FCSTD DOCUMENT  (FreeCAD 0.19R)
Label: HDprac
License: All rights reserved
LicenseURL: http://en.wikipedia.org/wiki/All_rights_reserved
objects: Part::Cylinder×62, Part::Refine×28, Part::Feature×24, Part::MultiFuse×22, Part::Cut×20, Part::FeaturePython×14, Part::Chamfer×9, App::Part×2, Part::Box×1
note: 180 computed .brp shape members not serialized (recipe doc carries the construction recipe); baked Part::Feature solids carry a one-line shape summary decoded from their .brp

FEATURE [Part::Feature] Part__Feature048  label="OUTPUT_SHAFT"
  Placement = pos=(0,0,-16) rot=(1,0,0;1.5708rad)
  shape: bbox 70.02 x 70.02 x 15.12 mm, 150 faces (baked)
FEATURE [Part::Feature] Part__Feature015  label="CIRCULAR_SPLINE"
  Placement = pos=(-3.943e-12,44,4.322e-12) rot=(1,0,0;3.14159rad)
  shape: bbox 100 x 10 x 100 mm, 706 faces (baked)
FEATURE [Part::Feature] Part__Feature014  label="FLEXGEAR"
  Placement = pos=(0,33.5,0) rot=(0,0,1;0rad)
  shape: bbox 81.18 x 57.96 x 81.18 mm, 699 faces (baked)
FEATURE [Part::FeaturePython] cycloidgear  # WARN: FeaturePython — macro-defined, semantics opaque (R4)
  AttacherType = Attacher::AttachEngine3D
  Placement = pos=(0,44,0) rot=(1,0,0;1.5708rad)
  backlash = 0
  beta = 0
  clearance = 0.25
  double_helix = false
  head = 0
  height = 10
  inner_diameter = 5
  module = 1
  numpoints = 15
  outer_diameter = 5
  teeth = 79
  version = 0.0.3
FEATURE [Part::Cylinder] Cylinder  label="Válec"
  Angle = 360
  AttacherType = Attacher::AttachEngine3D
  Height = 10
  Placement = pos=(0,44,0) rot=(1,0,0;1.5708rad)
  Radius = 50
FEATURE [Part::Cylinder] Cylinder001  label="Válec001"
  Angle = 360
  AttacherType = Attacher::AttachEngine3D
  Height = 10
  Placement = pos=(0,44,45.4) rot=(1,0,0;1.5708rad)
  Radius = 2.15
FEATURE [Part::Refine] Cylinder001001  label="Válec002"
  Placement = pos=(0,0,0) rot=(0,1,0;1.0472rad)
  Source = -> Cylinder001
FEATURE [Part::Refine] Cylinder001002  label="Válec003"
  Placement = pos=(0,0,0) rot=(0,1,0;2.0944rad)
  Source = -> Cylinder001
FEATURE [Part::Refine] Cylinder001003  label="Válec004"
  Placement = pos=(0,0,0) rot=(0,1,0;3.14159rad)
  Source = -> Cylinder001
FEATURE [Part::Refine] Cylinder001004  label="Válec005"
  Placement = pos=(0,0,0) rot=(0,1,0;4.18879rad)
  Source = -> Cylinder001
FEATURE [Part::Refine] Cylinder001005  label="Válec006"
  Placement = pos=(0,0,0) rot=(0,-1,0;1.0472rad)
  Source = -> Cylinder001
FEATURE [Part::MultiFuse] Fusion
  Shapes = -> [cycloidgear,Cylinder001,Cylinder001001,Cylinder001002,Cylinder001003,Cylinder001004,Cylinder001005]
FEATURE [Part::Chamfer] Chamfer
  Base = -> Cylinder
  Edges = 2 edges r=1: [Edge1,Edge3]
FEATURE [Part::Cut] Cut  label="CIRCULAR_79"
  Base = -> Chamfer
  Tool = -> Fusion
FEATURE [Part::Cylinder] Cylinder001006  label="Válec007"
  Angle = 360
  AttacherType = Attacher::AttachEngine3D
  Height = 10
  Placement = pos=(0,44,0) rot=(1,0,0;1.5708rad)
  Radius = 50
FEATURE [Part::FeaturePython] cycloidgear001  # WARN: FeaturePython — macro-defined, semantics opaque (R4)
  AttacherType = Attacher::AttachEngine3D
  Placement = pos=(0,43.5,0) rot=(1,0,0;1.5708rad)
  backlash = 0
  beta = 0
  clearance = 0.25
  double_helix = false
  head = 0
  height = 11
  inner_diameter = 5
  module = 0.55
  numpoints = 15
  outer_diameter = 5
  teeth = 145
  version = 0.0.3
FEATURE [Part::Cylinder] Cylinder001007  label="Válec008"
  Angle = 360
  AttacherType = Attacher::AttachEngine3D
  Height = 10
  Placement = pos=(0,44,45.4) rot=(1,0,0;1.5708rad)
  Radius = 2.15
FEATURE [Part::Chamfer] Chamfer001
  Base = -> Cylinder001006
  Edges = 2 edges r=1: [Edge1,Edge3]
FEATURE [Part::Refine] Cylinder001008  label="Válec009"
  Placement = pos=(0,0,0) rot=(0,1,0;2.0944rad)
  Source = -> Cylinder001007
FEATURE [Part::Refine] Cylinder001009  label="Válec010"
  Placement = pos=(0,0,0) rot=(0,1,0;1.0472rad)
  Source = -> Cylinder001007
FEATURE [Part::Refine] Cylinder001010  label="Válec011"
  Placement = pos=(0,0,0) rot=(0,1,0;4.18879rad)
  Source = -> Cylinder001007
FEATURE [Part::Refine] Cylinder001011  label="Válec012"
  Placement = pos=(0,0,0) rot=(0,-1,0;1.0472rad)
  Source = -> Cylinder001007
FEATURE [Part::Refine] Cylinder001012  label="Válec013"
  Placement = pos=(0,0,0) rot=(0,1,0;3.14159rad)
  Source = -> Cylinder001007
FEATURE [Part::MultiFuse] Fusion001
  Shapes = -> [cycloidgear001,Cylinder001007,Cylinder001009,Cylinder001008,Cylinder001012,Cylinder001010,Cylinder001011]
FEATURE [Part::Cut] Cut001  label="CIRCULAR_145"
  Base = -> Chamfer001
  Tool = -> Fusion001
FEATURE [Part::Cylinder] Cylinder001014  label="Válec015"
  Angle = 360
  AttacherType = Attacher::AttachEngine3D
  Height = 10
  Placement = pos=(0,44,0) rot=(1,0,0;1.5708rad)
  Radius = 50
FEATURE [Part::Cylinder] Cylinder001017  label="Válec018"
  Angle = 360
  AttacherType = Attacher::AttachEngine3D
  Height = 10
  Placement = pos=(0,44,45.4) rot=(1,0,0;1.5708rad)
  Radius = 2.15
FEATURE [Part::Refine] Cylinder001013  label="Válec014"
  Placement = pos=(0,0,0) rot=(0,-1,0;1.0472rad)
  Source = -> Cylinder001017
FEATURE [Part::Refine] Cylinder001015  label="Válec016"
  Placement = pos=(0,0,0) rot=(0,1,0;2.0944rad)
  Source = -> Cylinder001017
FEATURE [Part::Refine] Cylinder001016  label="Válec017"
  Placement = pos=(0,0,0) rot=(0,1,0;4.18879rad)
  Source = -> Cylinder001017
FEATURE [Part::FeaturePython] cycloidgear002  # WARN: FeaturePython — macro-defined, semantics opaque (R4)
  AttacherType = Attacher::AttachEngine3D
  Placement = pos=(0,44,0) rot=(1,0,0;1.5708rad)
  backlash = 0
  beta = 30
  clearance = 0.25
  double_helix = false
  head = 0
  height = 10
  inner_diameter = 5
  module = 0.792
  numpoints = 15
  outer_diameter = 5
  teeth = 101
  version = 0.0.3
FEATURE [Part::Chamfer] Chamfer002
  Base = -> Cylinder001014
  Edges = 2 edges r=1: [Edge1,Edge3]
FEATURE [Part::Refine] Cylinder001018  label="Válec019"
  Placement = pos=(0,0,0) rot=(0,1,0;1.0472rad)
  Source = -> Cylinder001017
FEATURE [Part::Refine] Cylinder001019  label="Válec020"
  Placement = pos=(0,0,0) rot=(0,1,0;3.14159rad)
  Source = -> Cylinder001017
FEATURE [Part::MultiFuse] Fusion002
  Shapes = -> [cycloidgear002,Cylinder001017,Cylinder001018,Cylinder001015,Cylinder001019,Cylinder001016,Cylinder001013]
FEATURE [Part::Cut] Cut002  label="CIRCULAR_101"
  Base = -> Chamfer002
  Tool = -> Fusion002
FEATURE [Part::FeaturePython] cycloidgear003  # WARN: FeaturePython — macro-defined, semantics opaque (R4)
  AttacherType = Attacher::AttachEngine3D
  Placement = pos=(0,44,0) rot=(1,0,0;1.5708rad)
  backlash = 0
  beta = 30
  clearance = 0.25
  double_helix = false
  head = 0
  height = 11
  inner_diameter = 5
  module = 0.792
  numpoints = 15
  outer_diameter = 5
  teeth = 101
  version = 0.0.3
FEATURE [Part::Cylinder] Cylinder001023  label="Válec024"
  Angle = 360
  AttacherType = Attacher::AttachEngine3D
  Height = 10
  Placement = pos=(0,44,45.4) rot=(1,0,0;1.5708rad)
  Radius = 2.15
FEATURE [Part::Refine] Cylinder001020  label="Válec021"
  Placement = pos=(0,0,0) rot=(0,1,0;4.18879rad)
  Source = -> Cylinder001023
FEATURE [Part::Refine] Cylinder001021  label="Válec022"
  Placement = pos=(0,0,0) rot=(0,-1,0;1.0472rad)
  Source = -> Cylinder001023
FEATURE [Part::Refine] Cylinder001022  label="Válec023"
  Placement = pos=(0,0,0) rot=(0,1,0;2.0944rad)
  Source = -> Cylinder001023
FEATURE [Part::Refine] Cylinder001024  label="Válec025"
  Placement = pos=(0,0,0) rot=(0,1,0;3.14159rad)
  Source = -> Cylinder001023
FEATURE [Part::Refine] Cylinder001025  label="Válec026"
  Placement = pos=(0,0,0) rot=(0,1,0;1.0472rad)
  Source = -> Cylinder001023
FEATURE [Part::MultiFuse] Fusion003
  Shapes = -> [cycloidgear003,Cylinder001023,Cylinder001025,Cylinder001022,Cylinder001024,Cylinder001020,Cylinder001021]
FEATURE [Part::Cylinder] Cylinder001026  label="Válec027"
  Angle = 360
  AttacherType = Attacher::AttachEngine3D
  Height = 10
  Placement = pos=(0,44,0) rot=(1,0,0;1.5708rad)
  Radius = 50
FEATURE [Part::Chamfer] Chamfer003
  Base = -> Cylinder001026
  Edges = 2 edges r=1: [Edge1,Edge3]
FEATURE [Part::Cut] Cut003
  Base = -> Chamfer003
  Tool = -> Fusion003
FEATURE [Part::Cylinder] cylinder
  Angle = 360
  AttacherType = Attacher::AttachEngine3D
  Height = 10
  Radius = 3
FEATURE [Part::Cylinder] cylinder001
  Angle = 360
  AttacherType = Attacher::AttachEngine3D
  Height = 10
  Placement = pos=(15,0,0) rot=(0,0,1;0rad)
  Radius = 3.5
FEATURE [Part::Cylinder] cylinder002
  Angle = 360
  AttacherType = Attacher::AttachEngine3D
  Height = 5
  Placement = pos=(15,0,0) rot=(0,0,1;0rad)
  Radius = 7
FEATURE [Part::Cylinder] cylinder003
  Angle = 360
  AttacherType = Attacher::AttachEngine3D
  Height = 10
  Placement = pos=(-15,0,0) rot=(0,0,1;0rad)
  Radius = 3.5
FEATURE [Part::Cylinder] cylinder004
  Angle = 360
  AttacherType = Attacher::AttachEngine3D
  Height = 5
  Placement = pos=(-15,0,0) rot=(0,0,1;0rad)
  Radius = 7
FEATURE [Part::Cylinder] cylinder005
  Angle = 360
  AttacherType = Attacher::AttachEngine3D
  Height = 10
  Placement = pos=(-25,0,0) rot=(0,0,1;0rad)
  Radius = 2.6
FEATURE [Part::Cylinder] cylinder006
  Angle = 360
  AttacherType = Attacher::AttachEngine3D
  Height = 10
  Placement = pos=(25,0,0) rot=(0,0,1;0rad)
  Radius = 2.6
FEATURE [Part::MultiFuse] union
  Shapes = -> [cylinder,cylinder001,cylinder002,cylinder003,cylinder004,cylinder005,cylinder006]
FEATURE [Part::Cylinder] Cylinder001027  label="Válec028"
  Angle = 360
  AttacherType = Attacher::AttachEngine3D
  Height = 10
  Radius = 35
FEATURE [Part::Cut] Cut004  label="H1"
  Base = -> Cylinder001027
  Placement = pos=(0,0,10) rot=(0,0,1;0rad)
  Tool = -> union
FEATURE [Part::Cylinder] Cylinder001028  label="H2"
  Angle = 360
  AttacherType = Attacher::AttachEngine3D
  Height = 10
  Radius = 35
FEATURE [Part::Cylinder] Cylinder001029  label="Válec030"
  Angle = 360
  AttacherType = Attacher::AttachEngine3D
  Height = 16
  Placement = pos=(0,24,-6) rot=(0,0,1;0rad)
  Radius = 2.15
FEATURE [Part::Cylinder] cylinder007
  Angle = 360
  AttacherType = Attacher::AttachEngine3D
  Height = 10
  Placement = pos=(-25,0,0) rot=(0,0,1;0rad)
  Radius = 2.6
FEATURE [Part::Cylinder] cylinder008
  Angle = 360
  AttacherType = Attacher::AttachEngine3D
  Height = 10
  Placement = pos=(25,0,0) rot=(0,0,1;0rad)
  Radius = 2.6
FEATURE [Part::Cylinder] cylinder009
  Angle = 360
  AttacherType = Attacher::AttachEngine3D
  Height = 10
  Radius = 3
FEATURE [Part::Cylinder] Cylinder001030  label="Válec031"
  Angle = 360
  AttacherType = Attacher::AttachEngine3D
  Height = 4
  Placement = pos=(0,24,6) rot=(0,0,1;0rad)
  Radius = 3.6
FEATURE [Part::MultiFuse] Fusion004  label="Imbus"
  Shapes = -> [Cylinder001030,Cylinder001029]
FEATURE [Part::Refine] Fusion004001  label="Imbus001"
  Placement = pos=(0,0,0) rot=(0,0,1;1.0472rad)
  Source = -> Fusion004
FEATURE [Part::Refine] Fusion004002  label="Imbus002"
  Placement = pos=(0,0,0) rot=(0,0,1;2.0944rad)
  Source = -> Fusion004
FEATURE [Part::Refine] Fusion004003  label="Imbus003"
  Placement = pos=(0,0,0) rot=(0,0,1;3.14159rad)
  Source = -> Fusion004
FEATURE [Part::Refine] Fusion004004  label="Imbus004"
  Placement = pos=(0,0,0) rot=(0,0,1;4.18879rad)
  Source = -> Fusion004
FEATURE [Part::Refine] Fusion004005  label="Imbus005"
  Placement = pos=(0,0,0) rot=(0,0,-1;1.0472rad)
  Source = -> Fusion004
FEATURE [Part::FeaturePython] Nut  label="M5-Nut"  # Fasteners workbench fastener (typed FeaturePython)
  Placement = pos=(25,0,0) rot=(0.894427,0,0.447214;0rad)
  diameter = 7
  invert = false
  matchOuter = false
  offset = 0
  thread = false
  type = 7
FEATURE [Part::FeaturePython] Nut001  label="M5-Nut001"  # Fasteners workbench fastener (typed FeaturePython)
  Placement = pos=(-25,0,0) rot=(0.894427,0,0.447214;0rad)
  diameter = 7
  invert = false
  matchOuter = false
  offset = 0
  thread = false
  type = 7
FEATURE [Part::MultiFuse] Fusion004006
  Shapes = -> [cylinder007,cylinder008,cylinder009,Fusion004,Fusion004001,Fusion004002,Fusion004003,Fusion004004,Fusion004005,Nut,Nut001]
FEATURE [Part::Cut] Cut005
  Base = -> Cylinder001028
  Tool = -> Fusion004006
FEATURE [Part::Chamfer] Chamfer004  label="HH1"
  Base = -> Cut004
  Edges = 2 edges r=1: [Edge1,Edge3]
FEATURE [Part::Chamfer] Chamfer005  label="HH2"
  Base = -> Cut005
  Edges = 2 edges r=1: [Edge1,Edge3]
FEATURE [Part::Feature] Part__Feature049  label="FLEXGEAR001"
  Placement = pos=(0,33.5,0) rot=(0,0,1;0rad)
  shape: bbox 81.18 x 57.96 x 81.18 mm, 699 faces (baked)
FEATURE [Part::FeaturePython] cycloidgear005  # WARN: FeaturePython — macro-defined, semantics opaque (R4)
  AttacherType = Attacher::AttachEngine3D
  Placement = pos=(0,43.5,0) rot=(1,0,0;1.5708rad)
  backlash = 0
  beta = 0
  clearance = 0.25
  double_helix = false
  head = 0
  height = 10.5
  inner_diameter = 5
  module = 0.79
  numpoints = 15
  outer_diameter = 5
  teeth = 100
  version = 0.0.3
FEATURE [Part::FeaturePython] Tube  # WARN: FeaturePython — macro-defined, semantics opaque (R4)
  AttacherType = Attacher::AttachEngine3D
  Height = 10
  InnerRadius = 36.5
  OuterRadius = 42
  Placement = pos=(0,35.75,0) rot=(1,0,0;1.5708rad)
FEATURE [Part::Chamfer] Chamfer007
  Base = -> Tube
  Edges = 1 edges r=4: [Edge5]
FEATURE [Part::Cut] Cut007
  Base = -> cycloidgear005
  Tool = -> Chamfer007
FEATURE [Part::Cylinder] Cylinder001038  label="Válec039"
  Angle = 360
  AttacherType = Attacher::AttachEngine3D
  Height = 10.5
  Placement = pos=(0,43.5,0) rot=(1,0,0;1.5708rad)
  Radius = 42
FEATURE [Part::Cylinder] Cylinder001039  label="Válec040"
  Angle = 360
  AttacherType = Attacher::AttachEngine3D
  Height = 10.5
  Placement = pos=(0,43.5,0) rot=(1,0,0;1.5708rad)
  Radius = 36.3
FEATURE [Part::Cut] Cut008
  Base = -> Part__Feature049
  Tool = -> Cylinder001038
FEATURE [Part::MultiFuse] Fusion004008
  Shapes = -> [Cut007,Cut008]
FEATURE [Part::Cut] Cut009  label="FLEX100"
  Base = -> Fusion004008
  Tool = -> Cylinder001039
FEATURE [Part::Refine] Cut009001  label="FLEX100n"
  Source = -> Cut009
FEATURE [Part::FeaturePython] cycloidgear006  # WARN: FeaturePython — macro-defined, semantics opaque (R4)
  AttacherType = Attacher::AttachEngine3D
  Placement = pos=(0,43.5,0) rot=(1,0,0;1.5708rad)
  backlash = 0
  beta = 0
  clearance = 0.25
  double_helix = false
  head = 0
  height = 10.5
  inner_diameter = 5
  module = 1
  numpoints = 15
  outer_diameter = 5
  teeth = 78
  version = 0.0.3
FEATURE [Part::Feature] Part__Feature050  label="FLEXGEAR002"
  Placement = pos=(0,33.5,0) rot=(0,0,1;0rad)
  shape: bbox 81.18 x 57.96 x 81.18 mm, 699 faces (baked)
FEATURE [Part::FeaturePython] Tube001  # WARN: FeaturePython — macro-defined, semantics opaque (R4)
  AttacherType = Attacher::AttachEngine3D
  Height = 10
  InnerRadius = 36.5
  OuterRadius = 42
  Placement = pos=(0,35.75,0) rot=(1,0,0;1.5708rad)
FEATURE [Part::Chamfer] Chamfer008
  Base = -> Tube001
  Edges = 1 edges r=4: [Edge5]
FEATURE [Part::Cut] Cut009002
  Base = -> cycloidgear006
  Tool = -> Chamfer008
FEATURE [Part::Cylinder] Cylinder001040  label="Válec041"
  Angle = 360
  AttacherType = Attacher::AttachEngine3D
  Height = 11.5
  Placement = pos=(0,43.5,0) rot=(1,0,0;1.5708rad)
  Radius = 36.3
FEATURE [Part::Cylinder] Cylinder001041  label="Válec042"
  Angle = 360
  AttacherType = Attacher::AttachEngine3D
  Height = 10.5
  Placement = pos=(0,43.5,0) rot=(1,0,0;1.5708rad)
  Radius = 42
FEATURE [Part::Cut] Cut009004
  Base = -> Part__Feature050
  Tool = -> Cylinder001041
FEATURE [Part::MultiFuse] Fusion004009
  Shapes = -> [Cut009002,Cut009004]
FEATURE [Part::Cut] Cut009003  label="FLEX78"
  Base = -> Fusion004009
  Tool = -> Cylinder001040
FEATURE [Part::Refine] Cut009003001  label="FLEX78n"
  Source = -> Cut009003
FEATURE [Part::FeaturePython] cycloidgear007  # WARN: FeaturePython — macro-defined, semantics opaque (R4)
  AttacherType = Attacher::AttachEngine3D
  Placement = pos=(0,43.5,0) rot=(1,0,0;1.5708rad)
  backlash = 0
  beta = 0
  clearance = 0.25
  double_helix = false
  head = 0
  height = 10.5
  inner_diameter = 5
  module = 0.55
  numpoints = 15
  outer_diameter = 5
  teeth = 144
  version = 0.0.3
FEATURE [Part::Feature] Part__Feature051  label="FLEXGEAR003"
  Placement = pos=(0,33.5,0) rot=(0,0,1;0rad)
  shape: bbox 81.18 x 57.96 x 81.18 mm, 699 faces (baked)
FEATURE [Part::FeaturePython] Tube002  # WARN: FeaturePython — macro-defined, semantics opaque (R4)
  AttacherType = Attacher::AttachEngine3D
  Height = 10
  InnerRadius = 36.5
  OuterRadius = 42
  Placement = pos=(0,35.75,0) rot=(1,0,0;1.5708rad)
FEATURE [Part::Chamfer] Chamfer009
  Base = -> Tube002
  Edges = 1 edges r=4: [Edge5]
FEATURE [Part::Cut] Cut009003002
  Base = -> cycloidgear007
  Tool = -> Chamfer009
FEATURE [Part::Cylinder] Cylinder001042  label="Válec043"
  Angle = 360
  AttacherType = Attacher::AttachEngine3D
  Height = 11.5
  Placement = pos=(0,43.5,0) rot=(1,0,0;1.5708rad)
  Radius = 36.3
FEATURE [Part::Cylinder] Cylinder001043  label="Válec044"
  Angle = 360
  AttacherType = Attacher::AttachEngine3D
  Height = 10.5
  Placement = pos=(0,43.5,0) rot=(1,0,0;1.5708rad)
  Radius = 42
FEATURE [Part::Cut] Cut009003004
  Base = -> Part__Feature051
  Tool = -> Cylinder001043
FEATURE [Part::MultiFuse] Fusion004010
  Shapes = -> [Cut009003002,Cut009003004]
FEATURE [Part::Cut] Cut009003003  label="FLEX144"
  Base = -> Fusion004010
  Tool = -> Cylinder001042
FEATURE [Part::Refine] Cut009003003001  label="FLEX144n"
  Source = -> Cut009003003
FEATURE [Part::Feature] Part__Feature030  label="MOTOR_CAP"
  Placement = pos=(0,0,0) rot=(0,1,0;0.523599rad)
  shape: bbox 106 x 12.2 x 106 mm, 94 faces (baked)
FEATURE [Part::Cylinder] Cylinder014005699  label="Válec616"
  Angle = 360
  AttacherType = Attacher::AttachEngine3D
  Height = 10
  Placement = pos=(-9.9,9.9,0) rot=(0,0,1;0rad)
  Radius = 1.6
FEATURE [Part::Cylinder] Cylinder014005700  label="Válec617"
  Angle = 360
  AttacherType = Attacher::AttachEngine3D
  Height = 10
  Placement = pos=(-9.9,-9.9,0) rot=(0,0,1;0rad)
  Radius = 1.6
FEATURE [Part::Cylinder] Cylinder014005701  label="Válec618"
  Angle = 360
  AttacherType = Attacher::AttachEngine3D
  Height = 10
  Placement = pos=(9.9,-9.9,0) rot=(0,0,1;0rad)
  Radius = 1.6
FEATURE [Part::Cylinder] Cylinder014005703  label="Válec619"
  Angle = 360
  AttacherType = Attacher::AttachEngine3D
  Height = 10
  Placement = pos=(9.9,9.9,0) rot=(0,0,1;0rad)
  Radius = 1.6
FEATURE [Part::MultiFuse] Fusion004011  label="Diry PG"
  Shapes = -> [Cylinder014005699,Cylinder014005703,Cylinder014005700,Cylinder014005701]
FEATURE [Part::Box] Box001  label="Krychle001"
  AttacherType = Attacher::AttachEngine3D
  Height = 40
  Length = 10
  Placement = pos=(43,39.5,-20) rot=(0,0,1;0rad)
  Width = 12
FEATURE [Part::Cylinder] Cylinder014005822  label="Válec735"
  Angle = 360
  AttacherType = Attacher::AttachEngine3D
  Height = 12
  Placement = pos=(0,51.5,0) rot=(1,0,0;1.5708rad)
  Radius = 51
FEATURE [Part::FeaturePython] Tube003  # WARN: FeaturePython — macro-defined, semantics opaque (R4)
  AttacherType = Attacher::AttachEngine3D
  Height = 4.5
  InnerRadius = 14
  OuterRadius = 30
  Placement = pos=(0,51.5,0) rot=(1,0,0;1.5708rad)
FEATURE [Part::Cut] Cut009003003003  label="Lista prac"
  Base = -> Box001
  Tool = -> Cylinder014005822
FEATURE [App::Part] Part
  Group = -> [Cylinder,cycloidgear,Fusion,Cylinder001,Chamfer,Cylinder001002,Cylinder001001,Cylinder001004,Cylinder001005,Cylinder001003,Cut,Cylinder001011,Cylinder001006,Cylinder001008,Cylinder001010,Cylinder001007,Fusion001,cycloidgear001,Chamfer001,Cylinder001009,Cylinder001012,Cut001,cycloidgear002,Fusion002,Cylinder001016,Cylinder001013,Cylinder001015,Cylinder001017,Cylinder001019,Chamfer002,+80 more]
  Origin = -> Origin
FEATURE [Part::Cylinder] Cylinder014005826  label="Válec739"
  Angle = 360
  AttacherType = Attacher::AttachEngine3D
  Height = 4
  Placement = pos=(0,17.5,0) rot=(0,0,1;0rad)
  Radius = 3.6
FEATURE [Part::Cylinder] Cylinder014005827  label="Válec740"
  Angle = 360
  AttacherType = Attacher::AttachEngine3D
  Height = 4
  Placement = pos=(-17.5,0,0) rot=(0,0,1;0rad)
  Radius = 3.6
FEATURE [Part::Cylinder] Cylinder014005828  label="Válec741"
  Angle = 360
  AttacherType = Attacher::AttachEngine3D
  Height = 4
  Placement = pos=(17.5,0,0) rot=(0,0,1;0rad)
  Radius = 3.6
FEATURE [Part::Cylinder] Cylinder014005834  label="Válec747"
  Angle = 360
  AttacherType = Attacher::AttachEngine3D
  Height = 4
  Placement = pos=(0,-17.5,0) rot=(0,0,1;0rad)
  Radius = 3.6
FEATURE [Part::MultiFuse] Fusion001089086  label="Diry HG002"
  Placement = pos=(0,0,-1) rot=(0,0,1;0rad)
  Shapes = -> [Cylinder014005828,Cylinder014005834,Cylinder014005827,Cylinder014005826]
FEATURE [Part::Cylinder] Cylinder014005835  label="Válec748"
  Angle = 360
  AttacherType = Attacher::AttachEngine3D
  Height = 10
  Placement = pos=(17.5,0,0) rot=(0,0,1;0rad)
  Radius = 2.15
FEATURE [Part::Cylinder] Cylinder014005836  label="Válec749"
  Angle = 360
  AttacherType = Attacher::AttachEngine3D
  Height = 10
  Placement = pos=(-17.5,0,0) rot=(0,0,1;0rad)
  Radius = 2.15
FEATURE [Part::Cylinder] Cylinder014005837  label="Válec750"
  Angle = 360
  AttacherType = Attacher::AttachEngine3D
  Height = 10
  Placement = pos=(0,17.5,0) rot=(0,0,1;0rad)
  Radius = 2.15
FEATURE [Part::Cylinder] Cylinder014005838  label="Válec751"
  Angle = 360
  AttacherType = Attacher::AttachEngine3D
  Height = 10
  Placement = pos=(0,-17.5,0) rot=(0,0,1;0rad)
  Radius = 2.15
FEATURE [Part::MultiFuse] Fusion001089087  label="Diry HG003"
  Shapes = -> [Cylinder014005835,Cylinder014005838,Cylinder014005836,Cylinder014005837]
FEATURE [Part::MultiFuse] Fusion001089085  label="GeerHD"
  Placement = pos=(0,47,0) rot=(-1,0,0;1.5708rad)
  Shapes = -> [Fusion001089087,Fusion001089086]
FEATURE [Part::Cylinder] Cylinder014005814  label="Válec727"
  Angle = 360
  AttacherType = Attacher::AttachEngine3D
  Height = 3
  Placement = pos=(9.9,9.9,0) rot=(0,0,1;0rad)
  Radius = 2.8
FEATURE [Part::Cylinder] Cylinder014005815  label="Válec728"
  Angle = 360
  AttacherType = Attacher::AttachEngine3D
  Height = 3
  Placement = pos=(9.9,-9.9,0) rot=(0,0,1;0rad)
  Radius = 2.8
FEATURE [Part::Cylinder] Cylinder014005816  label="Válec729"
  Angle = 360
  AttacherType = Attacher::AttachEngine3D
  Height = 3
  Placement = pos=(-9.9,-9.9,0) rot=(0,0,1;0rad)
  Radius = 2.8
FEATURE [Part::Cylinder] Cylinder014005817  label="Válec730"
  Angle = 360
  AttacherType = Attacher::AttachEngine3D
  Height = 3
  Placement = pos=(-9.9,9.9,0) rot=(0,0,1;0rad)
  Radius = 2.8
FEATURE [Part::MultiFuse] Fusion001089081  label="Diry PG001"
  Shapes = -> [Cylinder014005817,Cylinder014005814,Cylinder014005816,Cylinder014005815]
FEATURE [Part::MultiFuse] Fusion001089083  label="GeerPG"
  Placement = pos=(0,47,0) rot=(-1,0,0;1.5708rad)
  Shapes = -> [Fusion004011,Fusion001089081]
FEATURE [Part::Feature] Part__Feature052  label="MOTOR_CAP001"
  Placement = pos=(0,0,0) rot=(0,1,0;0.523599rad)
  shape: bbox 106 x 12.2 x 106 mm, 94 faces (baked)
FEATURE [Part::Cut] Cut009003003004  label="MotorPG"
  Base = -> Part__Feature052
  Tool = -> Fusion001089083
FEATURE [Part::Feature] Cut005_solid  label="Planetary Gear Box distance  RA"
  shape: bbox 41 x 41 x 22.5 mm, 15 faces (baked)
FEATURE [Part::Cylinder] Cylinder014005839  label="Válec752"
  Angle = 360
  AttacherType = Attacher::AttachEngine3D
  Height = 22.5
  Placement = pos=(15.5,15.5,0) rot=(0,0,1;0rad)
  Radius = 1.3
FEATURE [Part::Cylinder] Cylinder014005840  label="Válec753"
  Angle = 360
  AttacherType = Attacher::AttachEngine3D
  Height = 22.5
  Placement = pos=(-15.5,15.5,0) rot=(0,0,1;0rad)
  Radius = 1.3
FEATURE [Part::Cylinder] Cylinder014005841  label="Válec754"
  Angle = 360
  AttacherType = Attacher::AttachEngine3D
  Height = 22.5
  Placement = pos=(15.5,-15.5,0) rot=(0,0,1;0rad)
  Radius = 1.3
FEATURE [Part::Cylinder] Cylinder014005842  label="Válec755"
  Angle = 360
  AttacherType = Attacher::AttachEngine3D
  Height = 22.5
  Placement = pos=(-15.5,-15.5,0) rot=(0,0,1;0rad)
  Radius = 1.3
FEATURE [Part::MultiFuse] Fusion001089088
  Shapes = -> [Cylinder014005839,Cylinder014005840,Cylinder014005841,Cylinder014005842]
FEATURE [Part::Cylinder] Cylinder014005843  label="Válec756"
  Angle = 360
  AttacherType = Attacher::AttachEngine3D
  Height = 22.5
  Placement = pos=(15.5,15.5,0) rot=(0,0,1;0rad)
  Radius = 2
FEATURE [Part::Cylinder] Cylinder014005844  label="Válec757"
  Angle = 360
  AttacherType = Attacher::AttachEngine3D
  Height = 22.5
  Placement = pos=(-15.5,15.5,0) rot=(0,0,1;0rad)
  Radius = 2
FEATURE [Part::Cylinder] Cylinder014005845  label="Válec758"
  Angle = 360
  AttacherType = Attacher::AttachEngine3D
  Height = 22.5
  Placement = pos=(15.5,-15.5,0) rot=(0,0,1;0rad)
  Radius = 2
FEATURE [Part::Cylinder] Cylinder014005846  label="Válec759"
  Angle = 360
  AttacherType = Attacher::AttachEngine3D
  Height = 22.5
  Placement = pos=(-15.5,-15.5,0) rot=(0,0,1;0rad)
  Radius = 2
FEATURE [Part::MultiFuse] Fusion001089089
  Shapes = -> [Cylinder014005843,Cylinder014005844,Cylinder014005845,Cylinder014005846,Cut005_solid]
FEATURE [Part::Cut] Cut009003003005  label="PlantH"
  Base = -> Fusion001089089
  Tool = -> Fusion001089088
FEATURE [Part::Feature] Part__Feature011  label="606ZZ003"
  Placement = pos=(17.9237,7,-21.3677) rot=(0.707107,0.707107,0;3.14159rad)
  shape: bbox 18.4 x 6 x 18.4 mm, 16 faces (baked)
FEATURE [Part::Feature] Part__Feature013  label="606ZZ005"
  Placement = pos=(17.9237,7,21.3677) rot=(0.707107,0.707107,0;3.14159rad)
  shape: bbox 18.4 x 6 x 18.4 mm, 16 faces (baked)
FEATURE [Part::Feature] Part__Feature012  label="606ZZ004"
  Placement = pos=(-17.9237,7,21.3677) rot=(0.707107,0.707107,0;3.14159rad)
  shape: bbox 18.4 x 6 x 18.4 mm, 16 faces (baked)
FEATURE [Part::Feature] Part__Feature005  label="SQ_NUT_M005"
  Placement = pos=(9.1,9.5075,-1e-15) rot=(0,0,1;1.5708rad)
  shape: bbox 3.1 x 7.8 x 7.8 mm, 7 faces (baked)
FEATURE [Part::Feature] Part__Feature009  label="M4x017"
  Placement = pos=(-12,9.5075,1.2e-14) rot=(0,0,1;1.5708rad)
  shape: bbox 14 x 7 x 7 mm, 5 faces (baked)
FEATURE [Part::Feature] Part__Feature001  label="WAVE_BEARING_CAP"
  Placement = pos=(-2e-15,14,0) rot=(0,-1,0;1.5708rad)
  shape: bbox 49.37 x 8.25 x 70.52 mm, 105 faces (baked)
FEATURE [Part::Feature] Part__Feature010  label="606ZZ002"
  Placement = pos=(-17.9237,7,-21.3677) rot=(0.707107,0.707107,0;3.14159rad)
  shape: bbox 18.4 x 6 x 18.4 mm, 16 faces (baked)
FEATURE [Part::Feature] Part__Feature008  label="M4x10"
  Placement = pos=(12,9.5075,-8e-15) rot=(0,0,-1;1.5708rad)
  shape: bbox 14 x 7 x 7 mm, 5 faces (baked)
FEATURE [Part::Feature] Part__Feature004  label="SQ_NUT_M4"
  Placement = pos=(-6,9.5075,1e-15) rot=(0,0,1;1.5708rad)
  shape: bbox 3.1 x 7.8 x 7.8 mm, 7 faces (baked)
FEATURE [Part::Feature] Part__Feature003  label="606ZZ001"
  Placement = pos=(1.1e-14,7,28.5) rot=(0.707107,0.707107,0;3.14159rad)
  shape: bbox 18.4 x 6 x 18.4 mm, 16 faces (baked)
FEATURE [Part::Feature] Part__Feature007  label="M4x016"
  Placement = pos=(-7.9e-15,15.25,-28.5) rot=(0,0,1;0rad)
  shape: bbox 5.5 x 18 x 5.5 mm, 5 faces (baked)
FEATURE [Part::Feature] Part__Feature  label="WAVE_BEARING_PLATE"
  shape: bbox 49.37 x 14 x 70.52 mm, 157 faces (baked)
FEATURE [Part::Feature] Part__Feature006  label="M4x15"
  Placement = pos=(1.2e-15,15.25,28.5) rot=(0,0,1;0rad)
  shape: bbox 5.5 x 18 x 5.5 mm, 5 faces (baked)
FEATURE [Part::Feature] Part__Feature002  label="606ZZ"
  Placement = pos=(-1.1e-14,7,-28.5) rot=(0.707107,0.707107,0;3.14159rad)
  shape: bbox 18.4 x 6 x 18.4 mm, 16 faces (baked)
FEATURE [App::Part] WAVE_GEN1_ASM
  Group = -> [Part__Feature,Part__Feature001,Part__Feature002,Part__Feature003,Part__Feature004,Part__Feature005,Part__Feature006,Part__Feature007,Part__Feature008,Part__Feature009,Part__Feature010,Part__Feature011,Part__Feature012,Part__Feature013]
  Origin = -> Origin001
  Placement = pos=(-2.4e-15,27.5,1.1e-15) rot=(0,1,0;3.14159rad)
FEATURE [Part::Feature] Part__Feature053  label="WAVE_BEARING_PLATE001"
  Placement = pos=(0,0,0) rot=(1,0,0;1.5708rad)
  shape: bbox 49.37 x 70.52 x 14 mm, 157 faces (baked)
FEATURE [Part::Cylinder] Cylinder014005847  label="Válec760"
  Angle = 360
  AttacherType = Attacher::AttachEngine3D
  Height = 14
  Radius = 4.15
FEATURE [Part::Cylinder] Cylinder014005848  label="Válec761"
  Angle = 360
  AttacherType = Attacher::AttachEngine3D
  Height = 3
  Placement = pos=(0,28.5,0) rot=(0,0,1;0rad)
  Radius = 2.9
FEATURE [Part::Cylinder] Cylinder014005849  label="Válec762"
  Angle = 360
  AttacherType = Attacher::AttachEngine3D
  Height = 3
  Placement = pos=(0,-28.5,0) rot=(0,0,1;0rad)
  Radius = 2.9
FEATURE [Part::MultiFuse] Fusion001089090
  Shapes = -> [Cylinder014005848,Cylinder014005849]
FEATURE [Part::Cylinder] Cylinder014005850  label="Válec763"
  Angle = 360
  AttacherType = Attacher::AttachEngine3D
  Height = 3
  Placement = pos=(0,27.9,0) rot=(0,0,1;0rad)
  Radius = 2.9
FEATURE [Part::Cylinder] Cylinder014005851  label="Válec764"
  Angle = 360
  AttacherType = Attacher::AttachEngine3D
  Height = 3
  Placement = pos=(0,-27.9,0) rot=(0,0,1;0rad)
  Radius = 2.9
FEATURE [Part::MultiFuse] Fusion001089091
  Placement = pos=(0,0,0) rot=(0,0,-1;0.698132rad)
  Shapes = -> [Cylinder014005850,Cylinder014005851]
FEATURE [Part::Cylinder] Cylinder014005852  label="Válec765"
  Angle = 360
  AttacherType = Attacher::AttachEngine3D
  Height = 3
  Placement = pos=(0,-27.9,0) rot=(0,0,1;0rad)
  Radius = 2.9
FEATURE [Part::Cylinder] Cylinder014005853  label="Válec766"
  Angle = 360
  AttacherType = Attacher::AttachEngine3D
  Height = 3
  Placement = pos=(0,27.9,0) rot=(0,0,1;0rad)
  Radius = 2.9
FEATURE [Part::MultiFuse] Fusion001089092
  Placement = pos=(0,0,0) rot=(0,0,1;0.698132rad)
  Shapes = -> [Cylinder014005853,Cylinder014005852]
FEATURE [Part::Cylinder] Cylinder014005854  label="Válec767"
  Angle = 360
  AttacherType = Attacher::AttachEngine3D
  Height = 30
  Placement = pos=(-15,0,9.5) rot=(0,1,0;1.5708rad)
  Radius = 2.65
FEATURE [Part::MultiFuse] Fusion001089093
  Shapes = -> [Cylinder014005847,Fusion001089090,Fusion001089091,Fusion001089092,Cylinder014005854]
FEATURE [Part::Cut] Cut009003003006  label="WaveGenA"
  Base = -> Part__Feature053
  Tool = -> Fusion001089093
FEATURE [Part::FeaturePython] Tube004  # WARN: FeaturePython — macro-defined, semantics opaque (R4)
  AttacherType = Attacher::AttachEngine3D
  Height = 3
  InnerRadius = 4.2
  OuterRadius = 8
FEATURE [Part::Cylinder] Cylinder014005855  label="Válec768"
  Angle = 360
  AttacherType = Attacher::AttachEngine3D
  Height = 1
  Radius = 7
FEATURE [Part::Cut] Cut009003003007  label="ring"
  Base = -> Tube004
  Tool = -> Cylinder014005855
